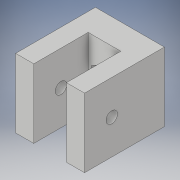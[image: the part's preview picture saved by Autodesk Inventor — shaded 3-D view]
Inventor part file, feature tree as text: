
AUTODESK INVENTOR PART (.ipt)
format: ipt  version: 2019 (Build 230136000, 136)  size: 284,160 bytes
history: native  units: in
note: dims shown in document units (in); Inventor stores cm internally (conversion verified against a paired STEP export)
features: extrude x5, sketch x5, projected_geometry x1
ambient origin geometry x8: Origin, YZ Plane, XZ Plane, XY Plane, X Axis, Y Axis, Z Axis, Center Point
bodies: Solid1 (feature_tree)
feature tree (11):
  extrude  "Extrusion1"  Depth=0.748in
  extrude  "Extrusion2"  Depth=0.3543in
  extrude  "Extrusion3"  Depth=0.5906in
  extrude  "Extrusion4"  Depth=0.5906in
  extrude  "Extrusion5"  Depth=0.126in
  sketch  "Sketch1"  dims[d0=0.748in d1=0.748in]
  sketch  "Sketch2"  dims[d2=0.2756in d3=0.0in d4=0.3543in]
  projected_geometry  "Projected Loop1"
  sketch  "Sketch3"  dims[d5=0.5906in d6=0.0in d7=0.1673in]
  sketch  "Sketch4"  dims[d8=0.5906in d9=0.0in d10=0.124in]
  sketch  "Sketch5"  dims[d11=0.5906in d12=0.0in d13=0.3248in d14=0.126in d15=0.0in]
